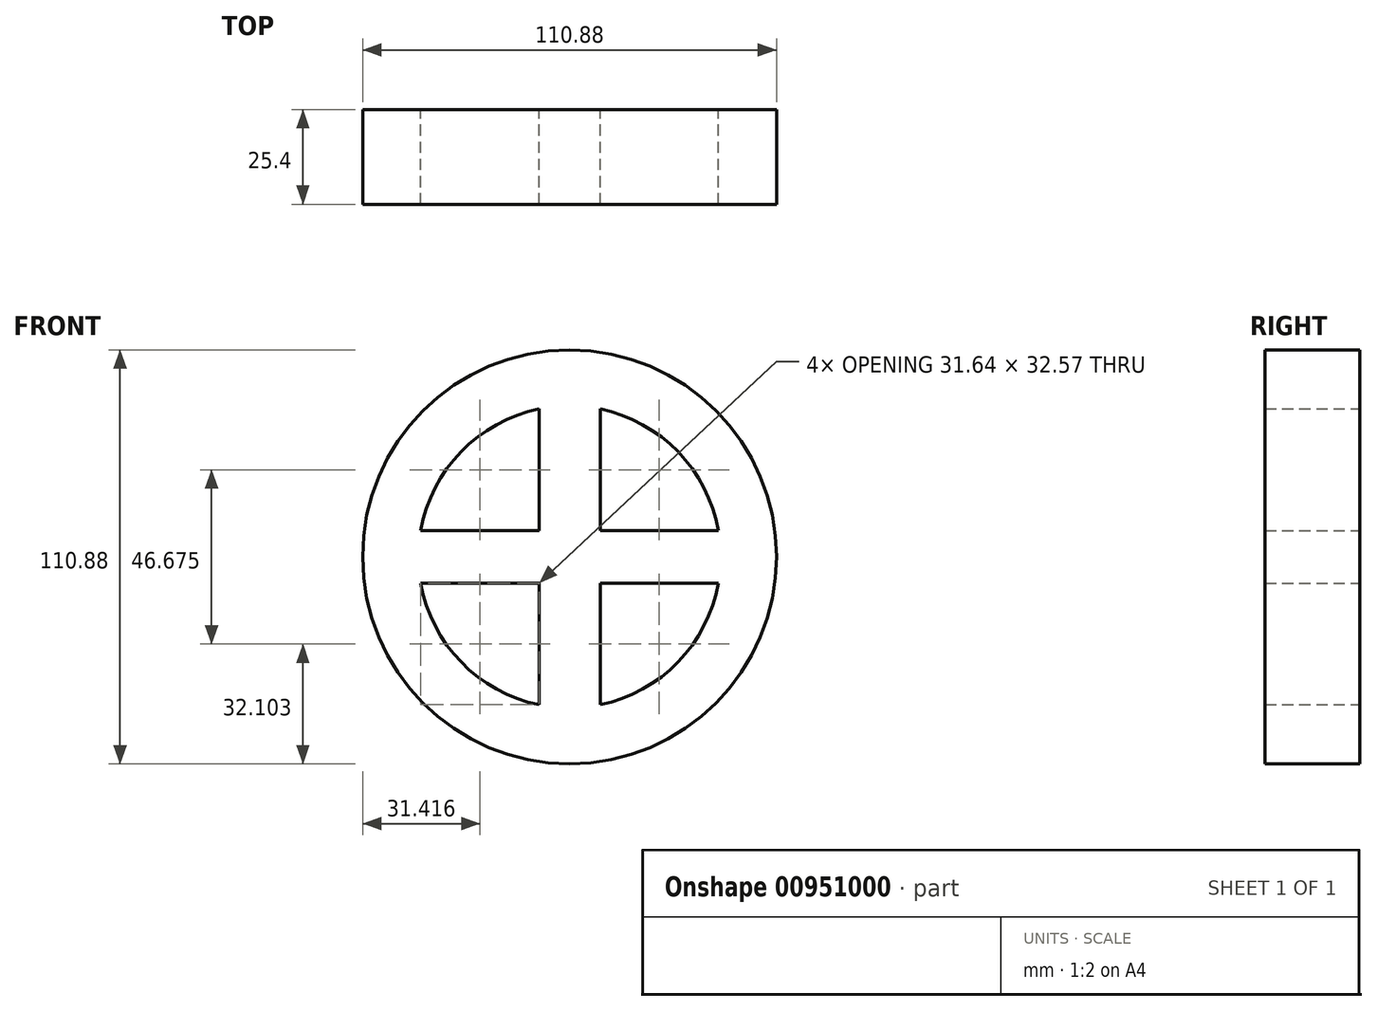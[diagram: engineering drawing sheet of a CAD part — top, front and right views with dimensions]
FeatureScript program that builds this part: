
annotation { "Feature Type Name" : "Feature", "Feature Type Description" : "" }
export const myFeature = defineFeature(function(context is Context, id is Id, definition is map)
    precondition{}
    {
        {
            var Q0;
            Q0=qCreatedBy(makeId("Front.planeOp"),FACE);
            var sketch = newSketch(context, id + "F0", { "sketchPlane" : qUnion([Q0])});
            skCircle(sketch, "E0", {"center": v(0, 0) * mm, "radius": 55.44 * mm});
            skCircle(sketch, "E1", {"center": v(0, 0) * mm, "radius": 40.46 * mm});
            skSolve(sketch);
        }
        {
            var Q0;
            Q0=makeQuery(id+"F0.imprint","IMPRINT",FACE,{"disambiguationData":[TD([[makeQuery(id+"F0.imprint","IMPRINT",EDGE,{"derivedFrom":sQuery(id+"F0.wireOp",EDGE,"E0")}),1.0]])]});
            extrude(context, id + "F1", {"entities" : qUnion([Q0]), "depth" : 25.4 * mm, "offsetDistance" : 25.4 * mm});
        }
        {
            var Q0;
            Q0=qCreatedBy(makeId("Front.planeOp"),FACE);
            var sketch = newSketch(context, id + "F2", { "sketchPlane" : qUnion([Q0])});
            skLineSegment(sketch, "E2.bottom", {"start": v(-42.74, -7.05) * mm, "end": v(42.74, -7.05) * mm});
            skLineSegment(sketch, "E2.top", {"start": v(-42.74, 7.05) * mm, "end": v(42.74, 7.05) * mm});
            skLineSegment(sketch, "E2.left", {"start": v(-42.74, -7.05) * mm, "end": v(-42.74, 7.05) * mm});
            skLineSegment(sketch, "E2.right", {"start": v(42.74, -7.05) * mm, "end": v(42.74, 7.05) * mm});
            skPoint(sketch, "E2.middle", {"position": v(0, 0) * mm});
            skSolve(sketch);
        }
        {
            var Q0;
            Q0=makeQuery(id+"F2.imprint","IMPRINT",FACE,{"disambiguationData":[TD([[makeQuery(id+"F2.imprint","IMPRINT",EDGE,{"derivedFrom":sQuery(id+"F2.wireOp",EDGE,"E2.bottom")}),1.0]])]});
            extrude(context, id + "F3", {"entities" : qUnion([Q0]), "operationType" : NewBodyOperationType.ADD, "depth" : 25.4 * mm, "offsetDistance" : 25.4 * mm});
        }
        {
            var Q0;
            Q0=qCreatedBy(makeId("Front.planeOp"),FACE);
            var sketch = newSketch(context, id + "F4", { "sketchPlane" : qUnion([Q0])});
            skLineSegment(sketch, "E3.bottom", {"start": v(8.2, -43.31) * mm, "end": v(-8.2, -43.31) * mm});
            skLineSegment(sketch, "E3.top", {"start": v(8.2, 43.31) * mm, "end": v(-8.2, 43.31) * mm});
            skLineSegment(sketch, "E3.left", {"start": v(8.2, -43.31) * mm, "end": v(8.2, 43.31) * mm});
            skLineSegment(sketch, "E3.right", {"start": v(-8.2, -43.31) * mm, "end": v(-8.2, 43.31) * mm});
            skPoint(sketch, "E3.middle", {"position": v(0, 0) * mm});
            skSolve(sketch);
        }
        {
            var Q0;
            Q0=makeQuery(id+"F4.imprint","IMPRINT",FACE,{"disambiguationData":[TD([[makeQuery(id+"F4.imprint","IMPRINT",EDGE,{"derivedFrom":sQuery(id+"F4.wireOp",EDGE,"E3.bottom")}),-1.0]])]});
            extrude(context, id + "F5", {"entities" : qUnion([Q0]), "operationType" : NewBodyOperationType.ADD, "depth" : 25.4 * mm, "offsetDistance" : 25.4 * mm});
        }
    });
